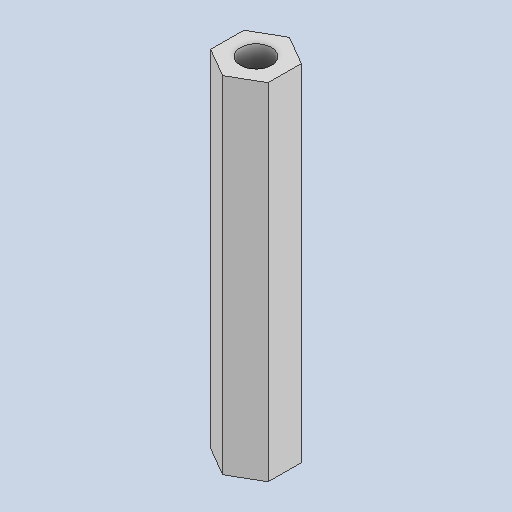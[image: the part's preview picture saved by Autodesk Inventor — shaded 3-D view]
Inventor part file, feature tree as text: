
AUTODESK INVENTOR PART (.ipt)
format: ipt  version: 2024 (Build 280153000, 153)  size: 87,040 bytes
history: native  units: in
note: dims shown in document units (in); Inventor stores cm internally (conversion verified against a paired STEP export)
features: other x3, sketch x1
ambient origin geometry x8: Origin, YZ Plane, XZ Plane, XY Plane, X Axis, Y Axis, Z Axis, Center Point
bodies: Solid1 (feature_tree)
feature tree (4):
  other  "Part4.ipt"
  other  "Solid1::Part4.ipt"
  other  "TaggingFeature1"
  sketch  "Sketch1"  dims[d0=0.3937in]
